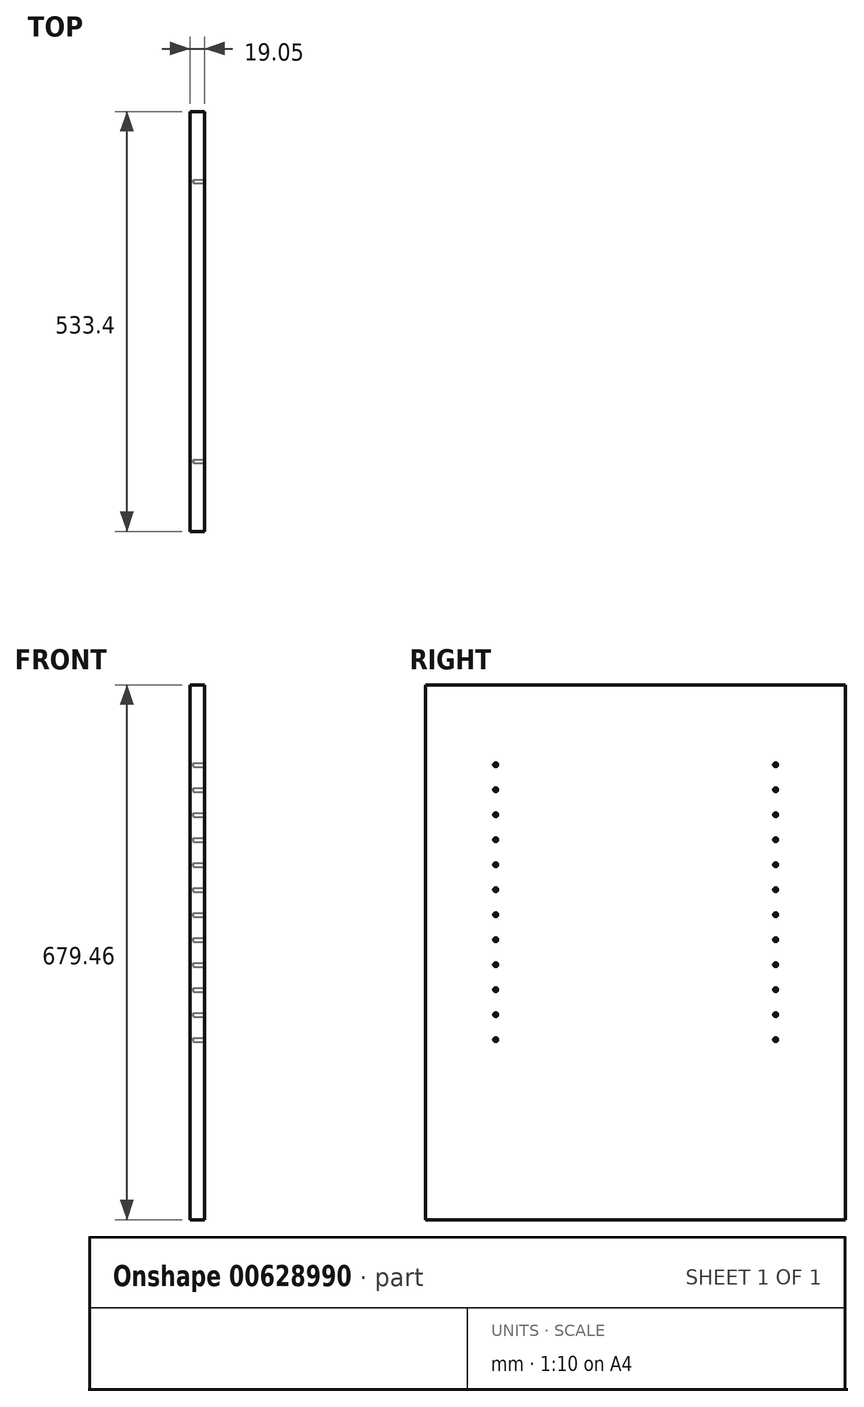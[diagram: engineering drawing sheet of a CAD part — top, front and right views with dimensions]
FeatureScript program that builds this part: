
annotation { "Feature Type Name" : "Feature", "Feature Type Description" : "" }
export const myFeature = defineFeature(function(context is Context, id is Id, definition is map)
    precondition{}
    {
        {
            var Q0;
            Q0=qCreatedBy(makeId("Right.planeOp"),FACE);
            var sketch = newSketch(context, id + "F0", { "sketchPlane" : qUnion([Q0])});
            skLineSegment(sketch, "E0.bottom", {"start": v(266.7, 339.73) * mm, "end": v(-266.7, 339.73) * mm});
            skLineSegment(sketch, "E0.top", {"start": v(266.7, -339.73) * mm, "end": v(-266.7, -339.73) * mm});
            skLineSegment(sketch, "E0.left", {"start": v(266.7, 339.73) * mm, "end": v(266.7, -339.73) * mm});
            skLineSegment(sketch, "E0.right", {"start": v(-266.7, 339.73) * mm, "end": v(-266.7, -339.73) * mm});
            skPoint(sketch, "E0.middle", {"position": v(0, 0) * mm});
            skSolve(sketch);
        }
        {
            var Q0;
            Q0=makeQuery(id+"F0.imprint","IMPRINT",FACE,{"disambiguationData":[TD([[makeQuery(id+"F0.imprint","IMPRINT",EDGE,{"derivedFrom":sQuery(id+"F0.wireOp",EDGE,"E0.bottom")}),1.0]])]});
            extrude(context, id + "F1", {"entities" : qUnion([Q0]), "depth" : 19.05 * mm, "offsetDistance" : 25.4 * mm});
        }
        {
            var Q0;
            Q0=makeQuery(id+"F1.opExtrude","CAP_FACE",FACE,{"disambiguationData":[OSD([sQuery(id+"F0.wireOp",EDGE,"E0.bottom"),sQuery(id+"F0.wireOp",EDGE,"E0.top"),sQuery(id+"F0.wireOp",EDGE,"E0.left"),sQuery(id+"F0.wireOp",EDGE,"E0.right")])],"isStart":false});
            var sketch = newSketch(context, id + "F2", { "sketchPlane" : qUnion([Q0])});
            skLineSegment(sketch, "E1", {"start": v(0, 339.73) * mm, "end": v(0, 206.38) * mm});
            skPoint(sketch, "E1.endSnap0", {"position": v(0, -339.73) * mm});
            skLineSegment(sketch, "E2.bottom", {"start": v(-177.8, 238.13) * mm, "end": v(177.8, 238.13) * mm});
            skLineSegment(sketch, "E2.top", {"start": v(-177.8, 174.63) * mm, "end": v(177.8, 174.63) * mm});
            skLineSegment(sketch, "E2.left", {"start": v(-177.8, 238.13) * mm, "end": v(-177.8, 174.63) * mm});
            skLineSegment(sketch, "E2.right", {"start": v(177.8, 238.13) * mm, "end": v(177.8, 174.63) * mm});
            skPoint(sketch, "E2.middle", {"position": v(0, 206.38) * mm});
            skLineSegment(sketch, "E3", {"start": v(0, 174.63) * mm, "end": v(0, 111.13) * mm});
            skPoint(sketch, "E3.endSnap0", {"position": v(0, 174.63) * mm});
            skLineSegment(sketch, "E4.bottom", {"start": v(-177.8, 79.38) * mm, "end": v(177.8, 79.38) * mm});
            skLineSegment(sketch, "E4.top", {"start": v(-177.8, 142.88) * mm, "end": v(177.8, 142.88) * mm});
            skLineSegment(sketch, "E4.left", {"start": v(-177.8, 79.38) * mm, "end": v(-177.8, 142.88) * mm});
            skLineSegment(sketch, "E4.right", {"start": v(177.8, 79.38) * mm, "end": v(177.8, 142.88) * mm});
            skPoint(sketch, "E4.middle", {"position": v(0, 111.13) * mm});
            skLineSegment(sketch, "E5", {"start": v(0, 79.38) * mm, "end": v(0, 15.88) * mm});
            skPoint(sketch, "E5.endSnap0", {"position": v(0, 79.38) * mm});
            skLineSegment(sketch, "E6.bottom", {"start": v(177.8, -15.87) * mm, "end": v(-177.8, -15.87) * mm});
            skLineSegment(sketch, "E6.top", {"start": v(177.8, 47.63) * mm, "end": v(-177.8, 47.63) * mm});
            skLineSegment(sketch, "E6.left", {"start": v(177.8, -15.87) * mm, "end": v(177.8, 47.63) * mm});
            skLineSegment(sketch, "E6.right", {"start": v(-177.8, -15.87) * mm, "end": v(-177.8, 47.62) * mm});
            skPoint(sketch, "E6.middle", {"position": v(0, 15.88) * mm});
            skLineSegment(sketch, "E7", {"start": v(0, -15.87) * mm, "end": v(0, -79.37) * mm});
            skLineSegment(sketch, "E8.bottom", {"start": v(-177.8, -111.12) * mm, "end": v(177.8, -111.12) * mm});
            skLineSegment(sketch, "E8.top", {"start": v(-177.8, -47.62) * mm, "end": v(177.8, -47.62) * mm});
            skLineSegment(sketch, "E8.left", {"start": v(-177.8, -111.12) * mm, "end": v(-177.8, -47.62) * mm});
            skLineSegment(sketch, "E8.right", {"start": v(177.8, -111.12) * mm, "end": v(177.8, -47.62) * mm});
            skPoint(sketch, "E8.middle", {"position": v(0, -79.37) * mm});
            skPoint(sketch, "E9", {"position": v(-177.8, 238.13) * mm});
            skPoint(sketch, "E10", {"position": v(-177.8, 206.38) * mm});
            skPoint(sketch, "E11", {"position": v(-177.8, 174.63) * mm});
            skPoint(sketch, "E12", {"position": v(-177.8, 142.88) * mm});
            skPoint(sketch, "E13", {"position": v(-177.8, 111.13) * mm});
            skPoint(sketch, "E14", {"position": v(-177.8, 79.38) * mm});
            skPoint(sketch, "E15", {"position": v(-177.8, 47.63) * mm});
            skPoint(sketch, "E16", {"position": v(-177.8, 15.88) * mm});
            skPoint(sketch, "E17", {"position": v(-177.8, -15.87) * mm});
            skPoint(sketch, "E18", {"position": v(-177.8, -47.62) * mm});
            skPoint(sketch, "E19", {"position": v(-177.8, -79.37) * mm});
            skPoint(sketch, "E20", {"position": v(-177.8, -111.12) * mm});
            skPoint(sketch, "E21", {"position": v(177.8, -111.12) * mm});
            skPoint(sketch, "E22", {"position": v(177.8, -79.37) * mm});
            skPoint(sketch, "E23", {"position": v(177.8, -47.62) * mm});
            skPoint(sketch, "E24", {"position": v(177.8, -15.87) * mm});
            skPoint(sketch, "E25", {"position": v(177.8, 15.88) * mm});
            skPoint(sketch, "E26", {"position": v(177.8, 47.63) * mm});
            skPoint(sketch, "E27", {"position": v(177.8, 79.38) * mm});
            skPoint(sketch, "E28", {"position": v(177.8, 111.13) * mm});
            skPoint(sketch, "E29", {"position": v(177.8, 142.88) * mm});
            skPoint(sketch, "E30", {"position": v(177.8, 238.13) * mm});
            skPoint(sketch, "E31", {"position": v(177.8, 206.38) * mm});
            skPoint(sketch, "E32", {"position": v(177.8, 174.63) * mm});
            skSolve(sketch);
        }
        {
            var Q0;
            Q0=sQuery(id+"F2.wireOp",VERTEX,"E9");
            var Q1;
            Q1=sQuery(id+"F2.wireOp",VERTEX,"E10");
            var Q2;
            Q2=sQuery(id+"F2.wireOp",VERTEX,"E11");
            var Q3;
            Q3=sQuery(id+"F2.wireOp",VERTEX,"E12");
            var Q4;
            Q4=sQuery(id+"F2.wireOp",VERTEX,"E13");
            var Q5;
            Q5=sQuery(id+"F2.wireOp",VERTEX,"E14");
            var Q6;
            Q6=sQuery(id+"F2.wireOp",VERTEX,"E15");
            var Q7;
            Q7=sQuery(id+"F2.wireOp",VERTEX,"E16");
            var Q8;
            Q8=sQuery(id+"F2.wireOp",VERTEX,"E17");
            var Q9;
            Q9=sQuery(id+"F2.wireOp",VERTEX,"E18");
            var Q10;
            Q10=sQuery(id+"F2.wireOp",VERTEX,"E19");
            var Q11;
            Q11=sQuery(id+"F2.wireOp",VERTEX,"E20");
            var Q12;
            Q12=sQuery(id+"F2.wireOp",VERTEX,"E30");
            var Q13;
            Q13=sQuery(id+"F2.wireOp",VERTEX,"E31");
            var Q14;
            Q14=sQuery(id+"F2.wireOp",VERTEX,"E32");
            var Q15;
            Q15=sQuery(id+"F2.wireOp",VERTEX,"E29");
            var Q16;
            Q16=sQuery(id+"F2.wireOp",VERTEX,"E28");
            var Q17;
            Q17=sQuery(id+"F2.wireOp",VERTEX,"E27");
            var Q18;
            Q18=sQuery(id+"F2.wireOp",VERTEX,"E26");
            var Q19;
            Q19=sQuery(id+"F2.wireOp",VERTEX,"E25");
            var Q20;
            Q20=sQuery(id+"F2.wireOp",VERTEX,"E24");
            var Q21;
            Q21=sQuery(id+"F2.wireOp",VERTEX,"E23");
            var Q22;
            Q22=sQuery(id+"F2.wireOp",VERTEX,"E22");
            var Q23;
            Q23=sQuery(id+"F2.wireOp",VERTEX,"E21");
            var Q24;
            Q24=makeQuery(id+"F1.opExtrude","SWEPT_BODY",BODY,{"disambiguationData":[OSD([sQuery(id+"F0.wireOp",EDGE,"E0.bottom"),sQuery(id+"F0.wireOp",EDGE,"E0.top"),sQuery(id+"F0.wireOp",EDGE,"E0.left"),sQuery(id+"F0.wireOp",EDGE,"E0.right")])]});
            hole(context, id + "F3", {"style" : HoleStyle.SIMPLE, "endStyle" : HoleEndStyle.BLIND, "holeDiameter" : 5 * mm, "majorDiameter" : 6.35 * mm, "holeDepth" : 14.22 * mm, "isTappedThrough" : true, "tappedDepth" : 12.7 * mm, "tapClearance" : 3, "startFromSketch" : true, "locations" : qUnion([Q0, Q1, Q2, Q3, Q4, Q5, Q6, Q7, Q8, Q9, Q10, Q11, Q12, Q13, Q14, Q15, Q16, Q17, Q18, Q19, Q20, Q21, Q22, Q23]), "scope" : qUnion([Q24])});
        }
    });
